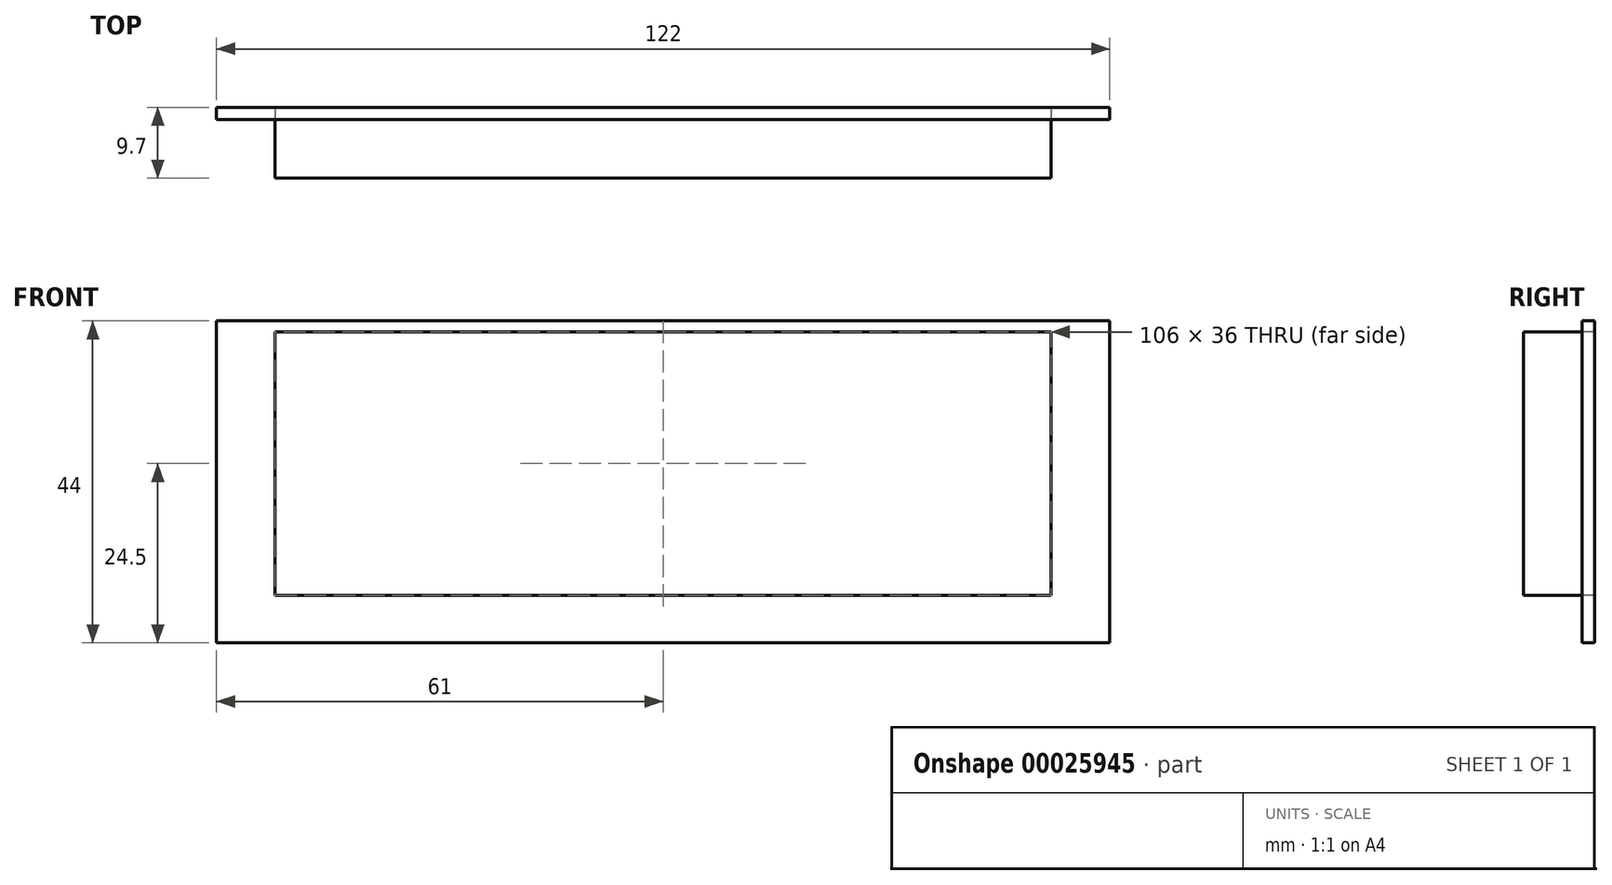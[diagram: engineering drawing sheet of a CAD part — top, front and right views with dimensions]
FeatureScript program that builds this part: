
annotation { "Feature Type Name" : "Feature", "Feature Type Description" : "" }
export const myFeature = defineFeature(function(context is Context, id is Id, definition is map)
    precondition{}
    {
        {
            var Q0;
            Q0=qCreatedBy(makeId("Front.planeOp"),FACE);
            var sketch = newSketch(context, id + "F0", { "sketchPlane" : qUnion([Q0])});
            skLineSegment(sketch, "E0.bottom", {"start": v(0, 0) * mm, "end": v(106, 0) * mm});
            skLineSegment(sketch, "E0.top", {"start": v(0, 36) * mm, "end": v(106, 36) * mm});
            skLineSegment(sketch, "E0.left", {"start": v(0, 0) * mm, "end": v(0, 36) * mm});
            skLineSegment(sketch, "E0.right", {"start": v(106, 0) * mm, "end": v(106, 36) * mm});
            skSolve(sketch);
        }
        {
            var Q0;
            Q0=makeQuery(id+"F0.imprint","IMPRINT",FACE,{"disambiguationData":[TD([[makeQuery(id+"F0.imprint","IMPRINT",EDGE,{"derivedFrom":sQuery(id+"F0.wireOp",EDGE,"E0.bottom")}),1.0]])]});
            extrude(context, id + "F1", {"entities" : qUnion([Q0]), "depth" : 8 * mm});
        }
        {
            var Q0;
            Q0=makeQuery(id+"F1.opExtrude","CAP_FACE",FACE,{"disambiguationData":[OSD([sQuery(id+"F0.wireOp",EDGE,"E0.bottom"),sQuery(id+"F0.wireOp",EDGE,"E0.top"),sQuery(id+"F0.wireOp",EDGE,"E0.left"),sQuery(id+"F0.wireOp",EDGE,"E0.right")])],"isStart":true});
            var sketch = newSketch(context, id + "F2", { "sketchPlane" : qUnion([Q0])});
            skLineSegment(sketch, "E1.bottom", {"start": v(-114, 37.5) * mm, "end": v(8, 37.5) * mm});
            skLineSegment(sketch, "E1.top", {"start": v(-114, -6.5) * mm, "end": v(8, -6.5) * mm});
            skLineSegment(sketch, "E1.left", {"start": v(-114, 37.5) * mm, "end": v(-114, -6.5) * mm});
            skLineSegment(sketch, "E1.right", {"start": v(8, 37.5) * mm, "end": v(8, -6.5) * mm});
            skSolve(sketch);
        }
        {
            var Q0;
            Q0=makeQuery(id+"F2.imprint","IMPRINT",FACE,{"disambiguationData":[TD([[makeQuery(id+"F2.imprint","IMPRINT",EDGE,{"derivedFrom":sQuery(id+"F2.wireOp",EDGE,"E1.bottom")}),-1.0]])]});
            extrude(context, id + "F3", {"entities" : qUnion([Q0]), "depth" : 1.7 * mm});
        }
    });
